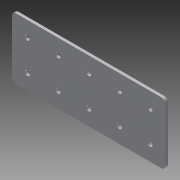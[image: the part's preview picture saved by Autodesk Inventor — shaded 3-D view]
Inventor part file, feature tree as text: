
AUTODESK INVENTOR PART (.ipt)
format: ipt  version: 2014 (Build 180170000, 170)  size: 111,616 bytes
history: native  units: in
note: dims shown in document units (in); Inventor stores cm internally (conversion verified against a paired STEP export)
features: sheet_metal_op x1, fillet x1, sketch x1, other x1
ambient origin geometry x8: Origin, YZ Plane, XZ Plane, XY Plane, X Axis, Y Axis, Z Axis, Center Point
bodies: Solid1 (feature_tree)
feature tree (4):
  sheet_metal_op  "Face1"
  fillet  "Fillet1"  Radius=5.0in
  sketch  "Sketch1"  dims[d1=2.0in d2=1.0in d3=0.164in d4=0.5in d5=1.9685in d7=1.0in d8=0.3937in d10=1.0in d12=0.5in d13=0.09in d14=0.125in]
  other  "Plate1"
